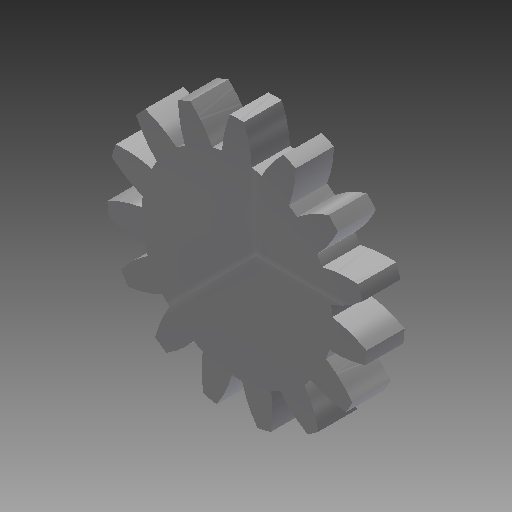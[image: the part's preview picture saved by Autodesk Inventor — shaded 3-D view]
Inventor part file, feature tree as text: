
AUTODESK INVENTOR PART (.ipt)
format: ipt  version: 2017 (Build 210142000, 142)  size: 197,120 bytes
history: native  units: mm (DEFAULTED — no unit token found)
features: plane x3, other x3, sketch x2, extrude x1
ambient origin geometry x8: Origin, YZ Plane, XZ Plane, XY Plane, X Axis, Y Axis, Z Axis, Center Point
bodies: Solid1 (feature_tree)
feature tree (9):
  extrude  "Extrusion1"  Depth=6.35mm TaperAngle=0.0deg
  plane  "Work Plane1"
  plane  "Work Plane2"
  plane  "Work Plane3"
  other  "Spur Gear"
  sketch  "Sketch1"  dims[d0=43.18mm d1=6.35mm d2=0.0mm]
  sketch  "Sketch2"  dims[d3=38.1mm d4=76.2mm d5=0.0mm d6=0.0mm d7=2.094395mm d9=0.0mm d14=0.0mm d15=181.61mm d16=0.0mm d17=0.0mm d18=0.0mm d19=181.61mm]
  other  "Srf1"
  other  "Pitch Diameter"
